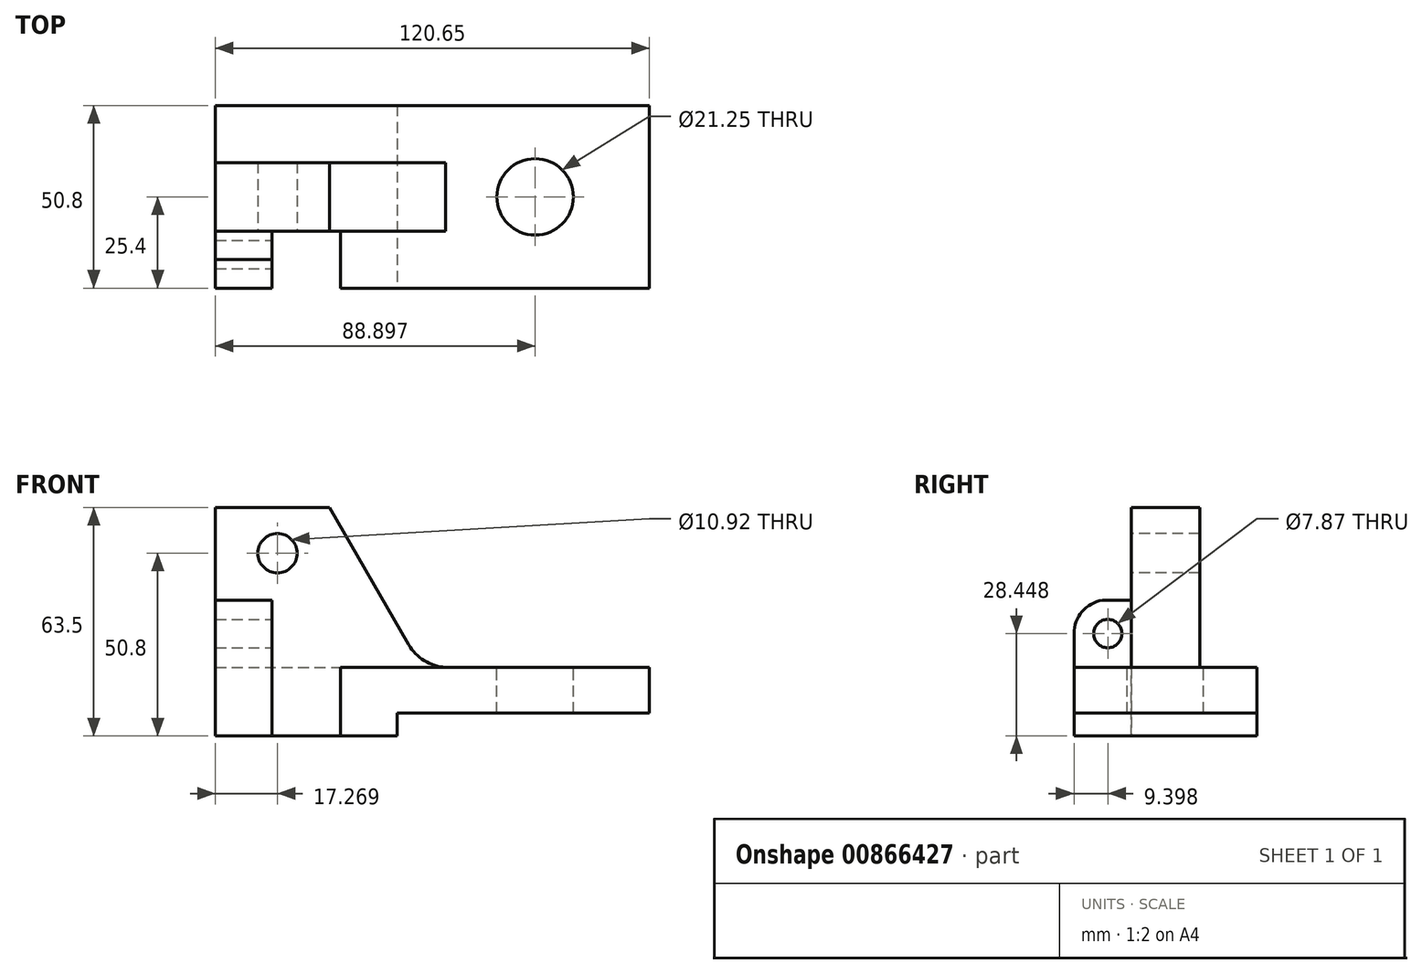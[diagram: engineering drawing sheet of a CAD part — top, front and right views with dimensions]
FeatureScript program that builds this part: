
annotation { "Feature Type Name" : "Feature", "Feature Type Description" : "" }
export const myFeature = defineFeature(function(context is Context, id is Id, definition is map)
    precondition{}
    {
        {
            var Q0;
            Q0=qCreatedBy(makeId("Top.planeOp"),FACE);
            var sketch = newSketch(context, id + "F0", { "sketchPlane" : qUnion([Q0])});
            skLineSegment(sketch, "E0.bottom", {"start": v(-59.96, 18.05) * mm, "end": v(60.69, 18.05) * mm});
            skLineSegment(sketch, "E0.top", {"start": v(-59.96, -32.75) * mm, "end": v(60.69, -32.75) * mm});
            skLineSegment(sketch, "E0.left", {"start": v(-59.96, 18.05) * mm, "end": v(-59.96, -32.75) * mm});
            skLineSegment(sketch, "E0.right", {"start": v(60.69, 18.05) * mm, "end": v(60.69, -32.75) * mm});
            skSolve(sketch);
        }
        {
            var Q0;
            Q0=makeQuery(id+"F0.imprint","IMPRINT",FACE,{"disambiguationData":[TD([[makeQuery(id+"F0.imprint","IMPRINT",EDGE,{"derivedFrom":sQuery(id+"F0.wireOp",EDGE,"E0.bottom")}),-1.0]])]});
            extrude(context, id + "F1", {"entities" : qUnion([Q0]), "depth" : 63.5 * mm, "offsetDistance" : 25.4 * mm});
        }
        {
            var Q0;
            Q0=makeQuery(id+"F1.opExtrude","SWEPT_FACE",FACE,{"disambiguationData":[OSD([sQuery(id+"F0.wireOp",EDGE,"E0.top")])]});
            var sketch = newSketch(context, id + "F2", { "sketchPlane" : qUnion([Q0])});
            skLineSegment(sketch, "E1", {"start": v(-25.17, 0) * mm, "end": v(-44.22, 0) * mm});
            skLineSegment(sketch, "E2", {"start": v(-25.17, 19.05) * mm, "end": v(-25.17, 0) * mm});
            skLineSegment(sketch, "E3", {"start": v(-59.96, 0) * mm, "end": v(-44.22, 0) * mm});
            skLineSegment(sketch, "E4", {"start": v(-59.96, 28.45) * mm, "end": v(-59.96, 0) * mm});
            skLineSegment(sketch, "E5", {"start": v(-9.42, 0) * mm, "end": v(-9.42, 6.35) * mm});
            skLineSegment(sketch, "E6", {"start": v(-9.42, 6.35) * mm, "end": v(60.69, 6.35) * mm});
            skLineSegment(sketch, "E7", {"start": v(-25.17, 19.05) * mm, "end": v(60.69, 19.05) * mm});
            skLineSegment(sketch, "E8", {"start": v(-44.22, 0) * mm, "end": v(-44.22, 28.45) * mm});
            skLineSegment(sketch, "E9", {"start": v(-44.22, 28.45) * mm, "end": v(-59.96, 28.45) * mm});
            skLineSegment(sketch, "E10", {"start": v(-59.96, 63.5) * mm, "end": v(-28.21, 63.5) * mm});
            skLineSegment(sketch, "E11", {"start": v(-44.22, 28.45) * mm, "end": v(-44.22, 44.91) * mm});
            skLineSegment(sketch, "E12", {"start": v(-44.22, 44.91) * mm, "end": v(-59.96, 44.91) * mm});
            skLineSegment(sketch, "E13", {"start": v(-28.21, 63.5) * mm, "end": v(-6.2, 25.38) * mm});
            skArc(sketch, "E14", {"start": v(-6.2, 25.38) * mm, "mid": v(-1.21, 20.54) * mm, "end": v(5.58, 19.05) * mm});
            skLineSegment(sketch, "E15", {"start": v(5.58, 19.05) * mm, "end": v(60.69, 19.05) * mm});
            skSolve(sketch);
        }
        {
            var Q0;
            {var subQ2=sQuery(id+"F2.wireOp",EDGE,"E13");Q0=makeQuery(id+"F2.imprint","IMPRINT",FACE,{"disambiguationData":[TD([[makeQuery(id+"F2.imprint","IMPRINT",EDGE,{"derivedFrom":subQ2}),1.0]])]});}
            var Q1;
            {var subQ0=sQuery(id+"F2.wireOp",EDGE,"E5");Q1=makeQuery(id+"F2.imprint","IMPRINT",FACE,{"disambiguationData":[TD([[makeQuery(id+"F2.imprint","IMPRINT",EDGE,{"derivedFrom":subQ0}),-1.0]])]});}
            extrude(context, id + "F3", {"entities" : qUnion([Q0, Q1]), "operationType" : NewBodyOperationType.REMOVE, "endBound" : BoundingType.THROUGH_ALL, "oppositeDirection" : true, "depth" : 25.4 * mm, "offsetDistance" : 25.4 * mm});
        }
        {
            var Q0;
            Q0=makeQuery(id+"F2.imprint","IMPRINT",FACE,{"disambiguationData":[TD([[makeQuery(id+"F2.imprint","IMPRINT",EDGE,{"derivedFrom":sQuery(id+"F2.wireOp",EDGE,"E1")}),1.0]])]});
            extrude(context, id + "F4", {"entities" : qUnion([Q0]), "operationType" : NewBodyOperationType.REMOVE, "oppositeDirection" : true, "depth" : 15.88 * mm, "offsetDistance" : 25.4 * mm});
        }
        {
            var Q0;
            Q0=makeQuery(id+"F1.opExtrude","SWEPT_FACE",FACE,{"disambiguationData":[OSD([sQuery(id+"F0.wireOp",EDGE,"E0.bottom")])]});
            var sketch = newSketch(context, id + "F5", { "sketchPlane" : qUnion([Q0])});
            skLineSegment(sketch, "E16", {"start": v(59.96, 19.05) * mm, "end": v(-15.97, 19.05) * mm});
            skSolve(sketch);
        }
        {
            var Q0;
            {var subQ0=sQuery(id+"F0.wireOp",EDGE,"E0.bottom");var subQ3=makeQuery(id+"F1.opExtrude","CAP_EDGE",EDGE,{"disambiguationData":[OSD([subQ0])],"isStart":false});Q0=makeQuery(id+"F5.imprint","IMPRINT",FACE,{"disambiguationData":[TD([[makeQuery(id+"F5.imprint","IMPRINT",EDGE,{"derivedFrom":subQ3}),1.0]])]});}
            extrude(context, id + "F6", {"entities" : qUnion([Q0]), "operationType" : NewBodyOperationType.REMOVE, "oppositeDirection" : true, "depth" : 15.88 * mm, "offsetDistance" : 25.4 * mm});
        }
        {
            var Q0;
            {var subQ0=sQuery(id+"F2.wireOp",EDGE,"E7");Q0=makeQuery(id+"F6.boolean.opBoolean","MERGE",FACE,{"derivedFrom":[makeQuery(id+"F4.boolean.opBoolean","MERGE",FACE,{"derivedFrom":[makeQuery(id+"F3.boolean.opBoolean","COPY",FACE,{"derivedFrom":makeQuery(id+"F3.opExtrude","SWEPT_FACE",FACE,{"disambiguationData":[OSD([subQ0,sQuery(id+"F2.wireOp",EDGE,"E15")])]})}),makeQuery(id+"F4.opExtrude","SWEPT_FACE",FACE,{"disambiguationData":[OSD([subQ0])]})]}),makeQuery(id+"F6.opExtrude","SWEPT_FACE",FACE,{"disambiguationData":[OSD([sQuery(id+"F5.wireOp",EDGE,"E16")])]})]});}
            var sketch = newSketch(context, id + "F7", { "sketchPlane" : qUnion([Q0])});
            skCircle(sketch, "E17", {"center": v(28.94, -7.35) * mm, "radius": 10.62 * mm});
            skSolve(sketch);
        }
        {
            var Q0;
            Q0=makeQuery(id+"F7.imprint","IMPRINT",FACE,{"disambiguationData":[TD([[makeQuery(id+"F7.imprint","IMPRINT",EDGE,{"derivedFrom":sQuery(id+"F7.wireOp",EDGE,"E17")}),1.0]])]});
            extrude(context, id + "F8", {"entities" : qUnion([Q0]), "operationType" : NewBodyOperationType.REMOVE, "endBound" : BoundingType.THROUGH_ALL, "oppositeDirection" : true, "depth" : 25.4 * mm, "offsetDistance" : 25.4 * mm});
        }
        {
            var Q0;
            Q0=makeQuery(id+"F4.boolean.opBoolean","COPY",FACE,{"derivedFrom":makeQuery(id+"F4.opExtrude","CAP_FACE",FACE,{"disambiguationData":[OSD([sQuery(id+"F0.wireOp",EDGE,"E0.top"),sQuery(id+"F0.wireOp",EDGE,"E0.left"),sQuery(id+"F2.wireOp",EDGE,"E1"),sQuery(id+"F2.wireOp",EDGE,"E2"),sQuery(id+"F2.wireOp",EDGE,"E7"),sQuery(id+"F2.wireOp",EDGE,"E8"),sQuery(id+"F2.wireOp",EDGE,"E10"),sQuery(id+"F2.wireOp",EDGE,"E11"),sQuery(id+"F2.wireOp",EDGE,"E12"),sQuery(id+"F2.wireOp",EDGE,"E13"),sQuery(id+"F2.wireOp",EDGE,"E14")])],"isStart":false})});
            var sketch = newSketch(context, id + "F9", { "sketchPlane" : qUnion([Q0])});
            skCircle(sketch, "E18", {"center": v(-42.7, 50.8) * mm, "radius": 5.46 * mm});
            skSolve(sketch);
        }
        {
            var Q0;
            Q0 = qSketchRegion(id + "F9", true);
            extrude(context, id + "F10", {"entities" : qUnion([Q0]), "operationType" : NewBodyOperationType.REMOVE, "oppositeDirection" : true, "depth" : 19.3 * mm, "offsetDistance" : 25.4 * mm});
        }
        {
            var Q0;
            Q0=makeQuery(id+"F1.opExtrude","SWEPT_FACE",FACE,{"disambiguationData":[OSD([sQuery(id+"F0.wireOp",EDGE,"E0.left")])]});
            var sketch = newSketch(context, id + "F11", { "sketchPlane" : qUnion([Q0])});
            skLineSegment(sketch, "E19", {"start": v(32.75, 28.45) * mm, "end": v(16.87, 28.45) * mm});
            skLineSegment(sketch, "E20", {"start": v(16.87, 44.91) * mm, "end": v(16.87, 28.45) * mm});
            skSolve(sketch);
        }
        {
            var Q0;
            {var subQ0=sQuery(id+"F11.wireOp",EDGE,"E19");Q0=makeQuery(id+"F11.imprint","IMPRINT",FACE,{"disambiguationData":[TD([[makeQuery(id+"F11.imprint","IMPRINT",EDGE,{"derivedFrom":subQ0}),-1.0]])]});}
            extrude(context, id + "F12", {"entities" : qUnion([Q0]), "operationType" : NewBodyOperationType.REMOVE, "endBound" : BoundingType.THROUGH_ALL, "oppositeDirection" : true, "depth" : 25.4 * mm, "offsetDistance" : 25.4 * mm});
        }
        {
            var Q0;
            Q0=makeQuery(id+"F1.opExtrude","SWEPT_FACE",FACE,{"disambiguationData":[OSD([sQuery(id+"F0.wireOp",EDGE,"E0.left")])]});
            var sketch = newSketch(context, id + "F13", { "sketchPlane" : qUnion([Q0])});
            skArc(sketch, "E21", {"start": v(32.75, 28.45) * mm, "mid": v(30.5, 34.56) * mm, "end": v(24.81, 37.73) * mm});
            skLineSegment(sketch, "E22", {"start": v(24.81, 37.73) * mm, "end": v(16.87, 37.73) * mm});
            skLineSegment(sketch, "E23", {"start": v(16.87, 37.73) * mm, "end": v(16.87, 28.45) * mm});
            skLineSegment(sketch, "E24", {"start": v(16.87, 28.45) * mm, "end": v(32.75, 28.45) * mm});
            skSolve(sketch);
        }
        {
            var Q0;
            Q0 = qSketchRegion(id + "F13", true);
            extrude(context, id + "F14", {"entities" : qUnion([Q0]), "operationType" : NewBodyOperationType.ADD, "oppositeDirection" : true, "depth" : 15.75 * mm, "offsetDistance" : 25.4 * mm});
        }
        {
            var Q0;
            Q0=makeQuery(id+"F14.boolean.opBoolean","MERGE",FACE,{"derivedFrom":[makeQuery(id+"F4.boolean.opBoolean","COPY",FACE,{"derivedFrom":makeQuery(id+"F4.opExtrude","SWEPT_FACE",FACE,{"disambiguationData":[OSD([sQuery(id+"F2.wireOp",EDGE,"E8"),sQuery(id+"F2.wireOp",EDGE,"E11")])]})}),makeQuery(id+"F14.opExtrude","CAP_FACE",FACE,{"disambiguationData":[OSD([sQuery(id+"F13.wireOp",EDGE,"E21"),sQuery(id+"F13.wireOp",EDGE,"E22"),sQuery(id+"F13.wireOp",EDGE,"E23"),sQuery(id+"F13.wireOp",EDGE,"E24")])],"isStart":false})]});
            var sketch = newSketch(context, id + "F15", { "sketchPlane" : qUnion([Q0])});
            skLineSegment(sketch, "E25", {"start": v(-32.75, 28.45) * mm, "end": v(-16.87, 28.45) * mm});
            skLineSegment(sketch, "E26", {"start": v(-16.87, 28.45) * mm, "end": v(-23.35, 28.45) * mm});
            skLineSegment(sketch, "E27", {"start": v(-23.35, 28.45) * mm, "end": v(-23.35, 37.73) * mm});
            skCircle(sketch, "E28", {"center": v(-23.35, 28.45) * mm, "radius": 3.94 * mm});
            skSolve(sketch);
        }
        {
            var Q0;
            Q0 = qSketchRegion(id + "F15", true);
            extrude(context, id + "F16", {"entities" : qUnion([Q0]), "operationType" : NewBodyOperationType.REMOVE, "endBound" : BoundingType.THROUGH_ALL, "oppositeDirection" : true, "depth" : 60.2 * mm, "offsetDistance" : 25.4 * mm});
        }
    });
